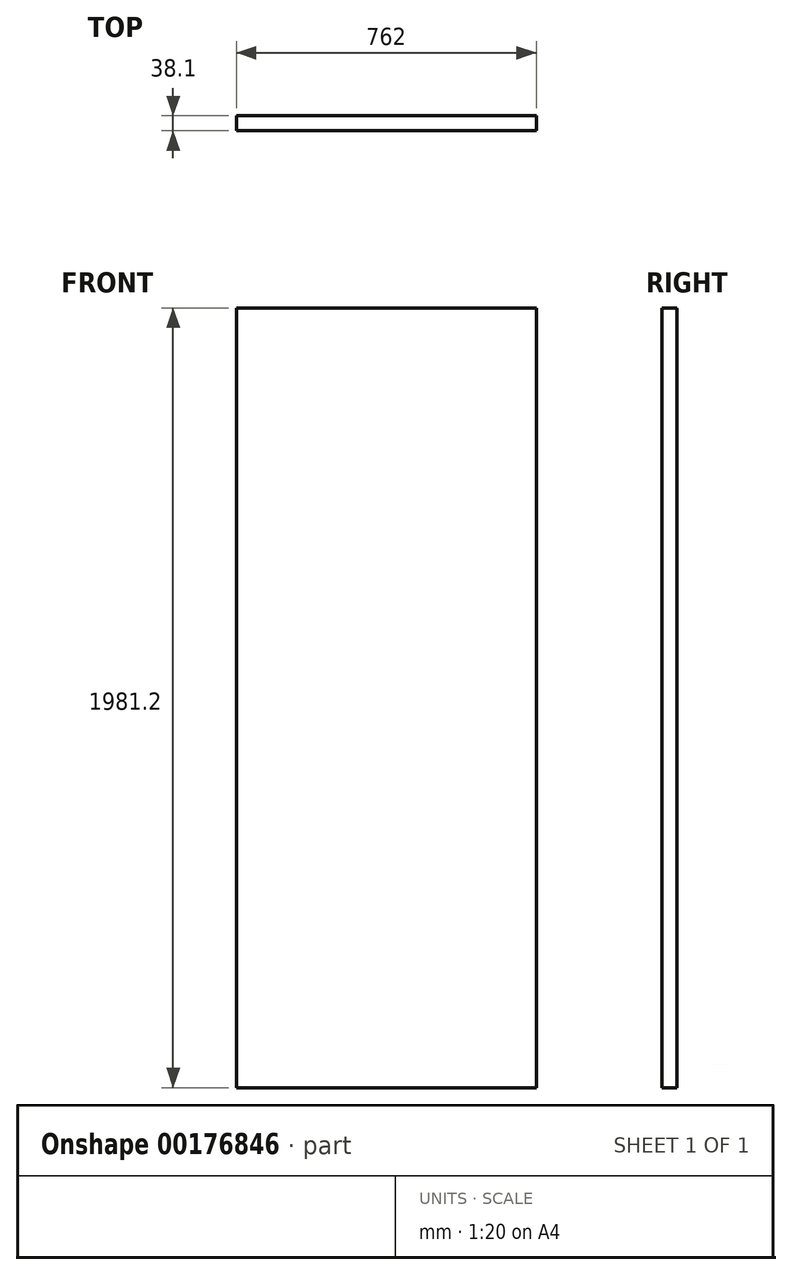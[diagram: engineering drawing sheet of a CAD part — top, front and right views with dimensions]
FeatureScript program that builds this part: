
annotation { "Feature Type Name" : "Feature", "Feature Type Description" : "" }
export const myFeature = defineFeature(function(context is Context, id is Id, definition is map)
    precondition{}
    {
        {
            var Q0;
            Q0=qCreatedBy(makeId("Top.planeOp"),FACE);
            var sketch = newSketch(context, id + "F0", { "sketchPlane" : qUnion([Q0])});
            skLineSegment(sketch, "E0.bottom", {"start": v(408.54, 19.05) * mm, "end": v(-353.46, 19.05) * mm});
            skLineSegment(sketch, "E0.top", {"start": v(408.54, -19.05) * mm, "end": v(-353.46, -19.05) * mm});
            skLineSegment(sketch, "E0.left", {"start": v(408.54, 19.05) * mm, "end": v(408.54, -19.05) * mm});
            skLineSegment(sketch, "E0.right", {"start": v(-353.46, 19.05) * mm, "end": v(-353.46, -19.05) * mm});
            skPoint(sketch, "E0.middle", {"position": v(27.54, 0) * mm});
            skSolve(sketch);
        }
        {
            var Q0;
            Q0=qSketchRegion(id+"F0",true);
            extrude(context, id + "F1", {"entities" : qUnion([Q0]), "depth" : 1981.2 * mm});
        }
    });
